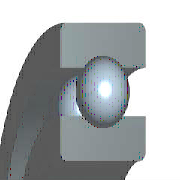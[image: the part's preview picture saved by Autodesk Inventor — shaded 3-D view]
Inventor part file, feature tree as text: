
AUTODESK INVENTOR PART (.ipt)
format: ipt  version: 2023.1 (Build 271208000, 208)  size: 276,992 bytes
history: native  units: mm (DEFAULTED — no unit token found)
features: sketch x1, other x1, pattern_circular x1
ambient origin geometry x8: Origin, YZ Plane, XZ Plane, XY Plane, X Axis, Y Axis, Z Axis, Center Point
bodies: Solid1 (feature_tree), Body (feature_tree)
feature tree (3):
  sketch  "Sketch"  dims[d0=7.02mm d6=90.0deg d7=90.0deg d1=1.0mm d2=110.0mm d3=360.0deg d4=0.0mm d5=0.0mm d8=0.0mm d9=35.0mm d11=62.0mm d12=14.0mm d13=43.802mm d14=0.0mm d15=0.0mm]
  other  "Ball"
  pattern_circular  "Balls"  Angle=90.0deg  [1 undecoded]
note: 1 required parameter value undecoded (feature->parameter linkage not recoverable at this tier; creation-order binding heuristic only, values carry confidence <= 0.55)
